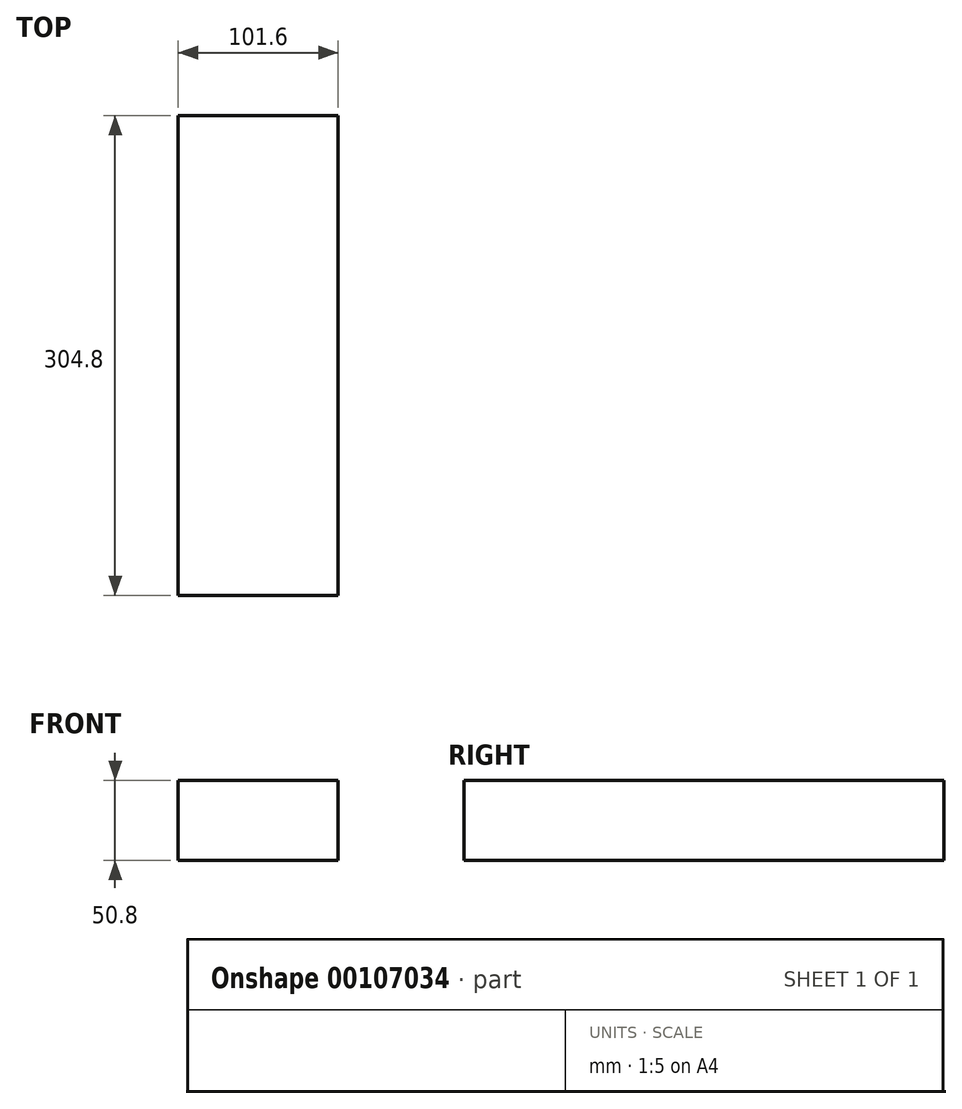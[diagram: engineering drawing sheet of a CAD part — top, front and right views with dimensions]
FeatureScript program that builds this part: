
annotation { "Feature Type Name" : "Feature", "Feature Type Description" : "" }
export const myFeature = defineFeature(function(context is Context, id is Id, definition is map)
    precondition{}
    {
        {
            var Q0;
            Q0=qCreatedBy(makeId("Top.planeOp"),FACE);
            var sketch = newSketch(context, id + "F0", { "sketchPlane" : qUnion([Q0])});
            skSolve(sketch);
        }
        {
            var Q0;
            Q0=qCreatedBy(makeId("Front.planeOp"),FACE);
            var sketch = newSketch(context, id + "F1", { "sketchPlane" : qUnion([Q0])});
            skLineSegment(sketch, "E0.bottom", {"start": v(-50.8, 25.4) * mm, "end": v(50.8, 25.4) * mm});
            skLineSegment(sketch, "E0.top", {"start": v(-50.8, -25.4) * mm, "end": v(50.8, -25.4) * mm});
            skLineSegment(sketch, "E0.left", {"start": v(-50.8, 25.4) * mm, "end": v(-50.8, -25.4) * mm});
            skLineSegment(sketch, "E0.right", {"start": v(50.8, 25.4) * mm, "end": v(50.8, -25.4) * mm});
            skSolve(sketch);
        }
        {
            var Q0;
            Q0 = qSketchRegion(id + "F0", true);
            var Q1;
            Q1 = qSketchRegion(id + "F1", true);
            extrude(context, id + "F2", {"entities" : qUnion([Q0, Q1]), "depth" : 304.8 * mm});
        }
    });
